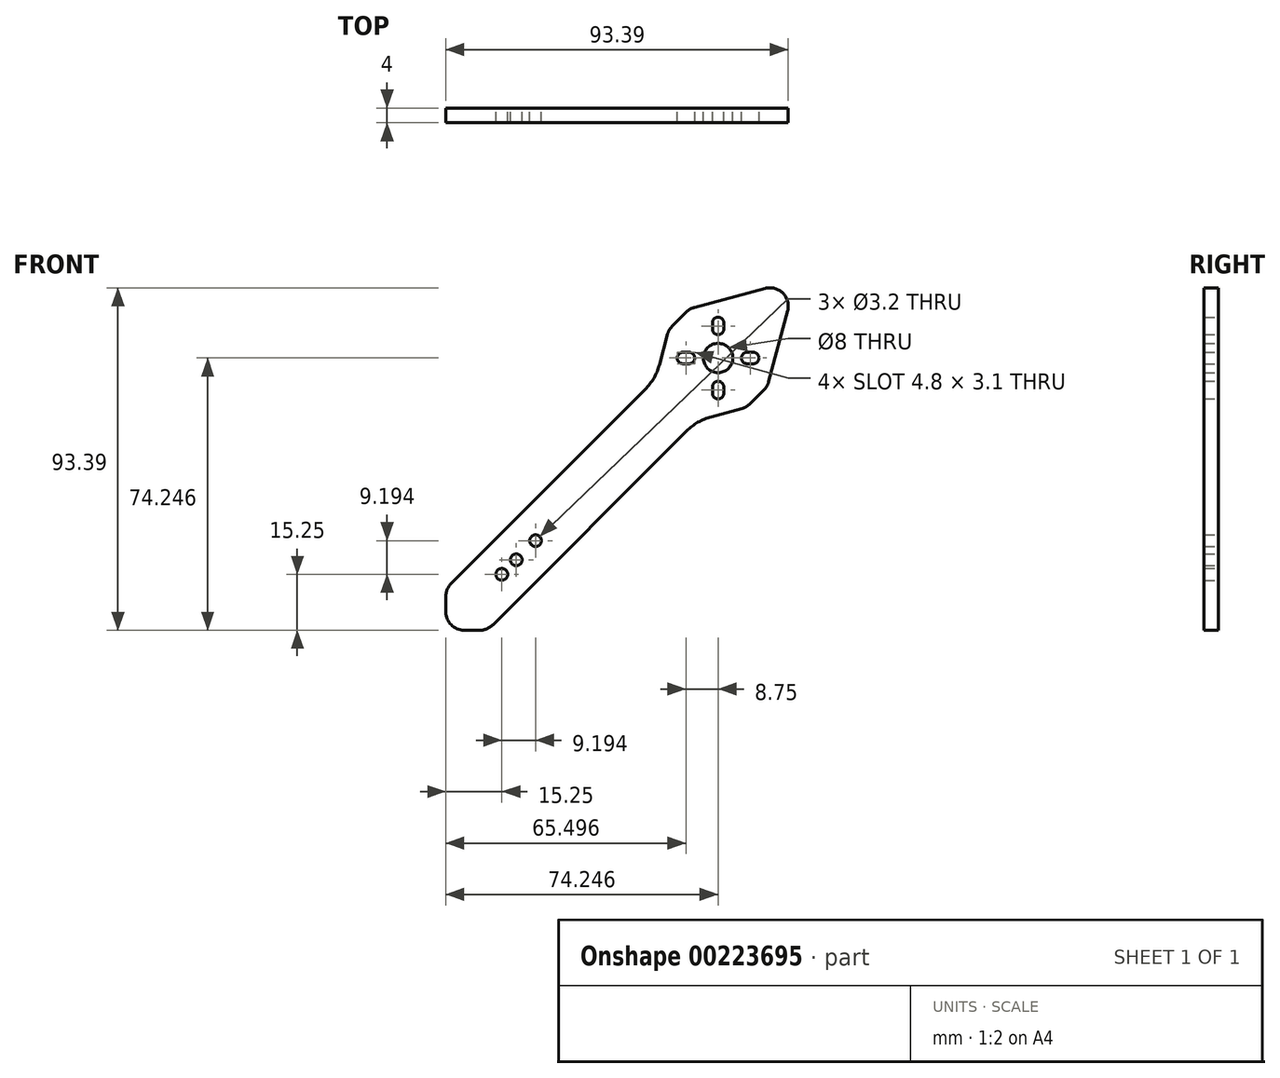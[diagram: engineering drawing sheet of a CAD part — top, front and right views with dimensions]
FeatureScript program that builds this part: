
annotation { "Feature Type Name" : "Feature", "Feature Type Description" : "" }
export const myFeature = defineFeature(function(context is Context, id is Id, definition is map)
    precondition{}
    {
        {
            var Q0;
            Q0=qCreatedBy(makeId("Front.planeOp"),FACE);
            var sketch = newSketch(context, id + "F0", { "sketchPlane" : qUnion([Q0])});
            skLineSegment(sketch, "E0", {"start": v(105.6, 105.6) * mm, "end": v(-91.93, -91.93) * mm, "construction": true});
            skLineSegment(sketch, "E1", {"start": v(53.41, 95.08) * mm, "end": v(99.76, 48.74) * mm, "construction": true});
            skPoint(sketch, "E2", {"position": v(0, 0) * mm});
            skCircle(sketch, "E3", {"center": v(74.25, 74.25) * mm, "radius": 4 * mm});
            skLineSegment(sketch, "E4", {"start": v(1.46, 12.78) * mm, "end": v(54.33, 65.65) * mm});
            skLineSegment(sketch, "E5", {"start": v(12.78, 1.46) * mm, "end": v(65.65, 54.33) * mm});
            skLineSegment(sketch, "E6", {"start": v(74.25, 40.06) * mm, "end": v(74.25, 102.92) * mm, "construction": true});
            skLineSegment(sketch, "E7", {"start": v(134.55, 74.25) * mm, "end": v(21.47, 74.25) * mm, "construction": true});
            skArc(sketch, "E8", {"start": v(75.8, 83.85) * mm, "mid": v(74.25, 85.4) * mm, "end": v(72.7, 83.85) * mm});
            skArc(sketch, "E9", {"start": v(72.7, 82.15) * mm, "mid": v(74.25, 80.6) * mm, "end": v(75.8, 82.15) * mm});
            skLineSegment(sketch, "E10", {"start": v(72.7, 83.85) * mm, "end": v(72.7, 82.15) * mm});
            skLineSegment(sketch, "E11.MirrorCS", {"start": v(75.8, 83.85) * mm, "end": v(75.8, 82.15) * mm});
            skArc(sketch, "E12.1.0", {"start": v(64.65, 75.8) * mm, "mid": v(63.1, 74.25) * mm, "end": v(64.65, 72.7) * mm});
            skLineSegment(sketch, "E12.1.1", {"start": v(64.65, 72.7) * mm, "end": v(66.35, 72.7) * mm});
            skLineSegment(sketch, "E12.1.2", {"start": v(64.65, 75.8) * mm, "end": v(66.35, 75.8) * mm});
            skArc(sketch, "E12.1.3", {"start": v(66.35, 72.7) * mm, "mid": v(67.9, 74.25) * mm, "end": v(66.35, 75.8) * mm});
            skArc(sketch, "E12.2.0", {"start": v(72.7, 64.65) * mm, "mid": v(74.25, 63.1) * mm, "end": v(75.8, 64.65) * mm});
            skLineSegment(sketch, "E12.2.1", {"start": v(75.8, 64.65) * mm, "end": v(75.8, 66.35) * mm});
            skLineSegment(sketch, "E12.2.2", {"start": v(72.7, 64.65) * mm, "end": v(72.7, 66.35) * mm});
            skArc(sketch, "E12.2.3", {"start": v(75.8, 66.35) * mm, "mid": v(74.25, 67.9) * mm, "end": v(72.7, 66.35) * mm});
            skArc(sketch, "E12.3.0", {"start": v(83.85, 72.7) * mm, "mid": v(85.4, 74.25) * mm, "end": v(83.85, 75.8) * mm});
            skLineSegment(sketch, "E12.3.1", {"start": v(83.85, 75.8) * mm, "end": v(82.15, 75.8) * mm});
            skLineSegment(sketch, "E12.3.2", {"start": v(83.85, 72.7) * mm, "end": v(82.15, 72.7) * mm});
            skArc(sketch, "E12.3.3", {"start": v(82.15, 75.8) * mm, "mid": v(80.6, 74.25) * mm, "end": v(82.15, 72.7) * mm});
            skLineSegment(sketch, "E13", {"start": v(61.74, 82.96) * mm, "end": v(65.53, 86.75) * mm});
            skLineSegment(sketch, "E14", {"start": v(82.96, 61.74) * mm, "end": v(86.75, 65.53) * mm});
            skPoint(sketch, "E15", {"position": v(95.46, 95.46) * mm});
            skLineSegment(sketch, "E16", {"start": v(67.78, 88.04) * mm, "end": v(87.1, 93.22) * mm});
            skLineSegment(sketch, "E17", {"start": v(88.04, 67.78) * mm, "end": v(93.22, 87.1) * mm});
            skLineSegment(sketch, "E18", {"start": v(57.97, 96.2) * mm, "end": v(99.95, 54.23) * mm, "construction": true});
            skArc(sketch, "E19.filletArc", {"start": v(93.22, 87.1) * mm, "mid": v(91.92, 91.92) * mm, "end": v(87.1, 93.22) * mm});
            skLineSegment(sketch, "E20", {"start": v(58.21, 72.37) * mm, "end": v(60.45, 80.72) * mm});
            skLineSegment(sketch, "E21", {"start": v(72.37, 58.21) * mm, "end": v(80.72, 60.45) * mm});
            skPoint(sketch, "E22.visualSharp", {"position": v(57.17, 68.49) * mm});
            skArc(sketch, "E22.filletArc", {"start": v(54.33, 65.65) * mm, "mid": v(56.72, 68.75) * mm, "end": v(58.21, 72.37) * mm});
            skPoint(sketch, "E23.visualSharp", {"position": v(68.49, 57.17) * mm});
            skArc(sketch, "E23.filletArc", {"start": v(72.37, 58.21) * mm, "mid": v(68.75, 56.72) * mm, "end": v(65.65, 54.33) * mm});
            skPoint(sketch, "E24.visualSharp", {"position": v(60.8, 82.01) * mm});
            skArc(sketch, "E24.filletArc", {"start": v(61.74, 82.96) * mm, "mid": v(60.95, 81.92) * mm, "end": v(60.45, 80.72) * mm});
            skPoint(sketch, "E25.visualSharp", {"position": v(66.48, 87.7) * mm});
            skArc(sketch, "E25.filletArc", {"start": v(67.78, 88.04) * mm, "mid": v(66.57, 87.54) * mm, "end": v(65.53, 86.75) * mm});
            skPoint(sketch, "E26.visualSharp", {"position": v(82.01, 60.8) * mm});
            skArc(sketch, "E26.filletArc", {"start": v(80.72, 60.45) * mm, "mid": v(81.92, 60.95) * mm, "end": v(82.96, 61.74) * mm});
            skPoint(sketch, "E27.visualSharp", {"position": v(87.7, 66.48) * mm});
            skArc(sketch, "E27.filletArc", {"start": v(86.75, 65.53) * mm, "mid": v(87.54, 66.57) * mm, "end": v(88.04, 67.78) * mm});
            skLineSegment(sketch, "E28", {"start": v(0, 9.24) * mm, "end": v(0, 5) * mm});
            skLineSegment(sketch, "E29", {"start": v(9.24, 0) * mm, "end": v(5, 0) * mm});
            skPoint(sketch, "E30.visualSharp", {"position": v(0, 11.31) * mm});
            skArc(sketch, "E30.filletArc", {"start": v(1.46, 12.78) * mm, "mid": v(0.38, 11.16) * mm, "end": v(0, 9.24) * mm});
            skPoint(sketch, "E31.visualSharp", {"position": v(11.31, 0) * mm});
            skArc(sketch, "E31.filletArc", {"start": v(9.24, 0) * mm, "mid": v(11.16, 0.38) * mm, "end": v(12.78, 1.46) * mm});
            skArc(sketch, "E32.filletArc", {"start": v(0, 5) * mm, "mid": v(1.46, 1.46) * mm, "end": v(5, 0) * mm});
            skCircle(sketch, "E33", {"center": v(15.25, 15.25) * mm, "radius": 1.6 * mm});
            skCircle(sketch, "E34", {"center": v(24.44, 24.44) * mm, "radius": 1.6 * mm});
            skCircle(sketch, "E35", {"center": v(19.21, 19.21) * mm, "radius": 1.6 * mm});
            skSolve(sketch);
        }
        {
            var Q0;
            Q0=qSketchRegion(id+"F0",true);
            extrude(context, id + "F1", {"entities" : qUnion([Q0]), "depth" : 4 * mm});
        }
    });
